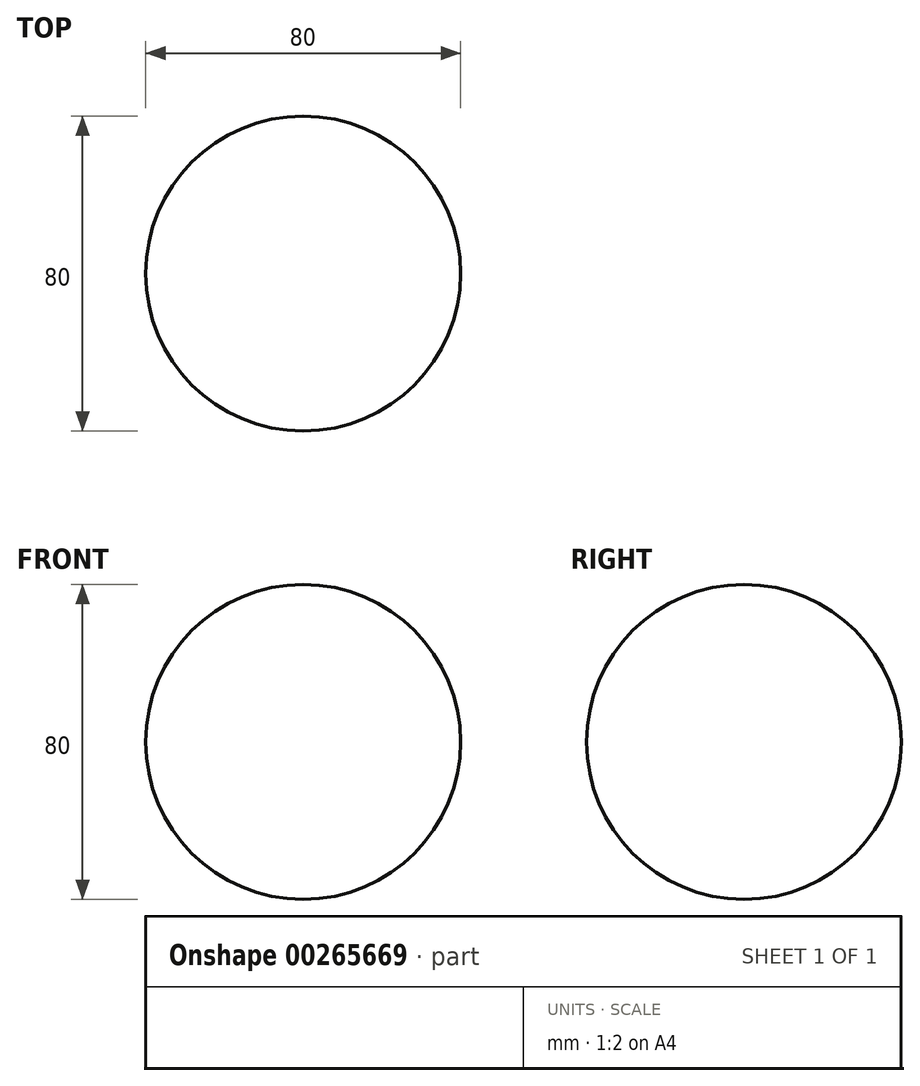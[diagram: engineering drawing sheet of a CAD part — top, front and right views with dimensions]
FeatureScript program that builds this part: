
annotation { "Feature Type Name" : "Feature", "Feature Type Description" : "" }
export const myFeature = defineFeature(function(context is Context, id is Id, definition is map)
    precondition{}
    {
        {
            var Q0;
            Q0=qCreatedBy(makeId("Front.planeOp"),FACE);
            var sketch = newSketch(context, id + "F0", { "sketchPlane" : qUnion([Q0])});
            skArc(sketch, "E0", {"start": v(0, 40) * mm, "mid": v(40, 0) * mm, "end": v(0, -40) * mm});
            skLineSegment(sketch, "E1", {"start": v(0, 58.92) * mm, "end": v(0, -54.96) * mm});
            skSolve(sketch);
        }
        {
            var Q0;
            Q0 = qSketchRegion(id + "F0", true);
            var Q1;
            Q1=sQuery(id+"F0.wireOp",EDGE,"E1");
            revolve(context, id + "F1", {"entities" : qUnion([Q0]), "axis" : qUnion([Q1]), "revolveType" : RevolveType.FULL});
        }
    });
